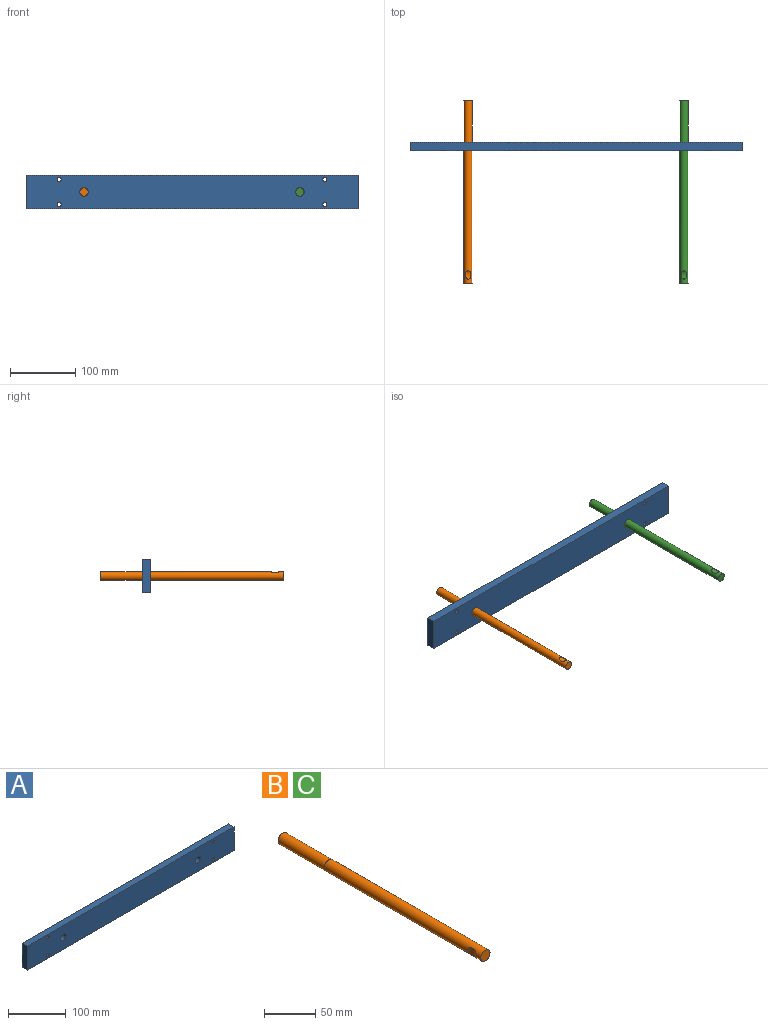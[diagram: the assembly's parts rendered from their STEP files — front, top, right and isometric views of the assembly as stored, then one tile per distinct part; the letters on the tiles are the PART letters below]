
ASSEMBLY  parts=3 mates=1
PART A: 12 faces, bbox 508x12.7x50.8 mm
  f0: plane 508x12.7mm, normal (0,0,-1), area 6451.6mm2, adj f1,f3,f4,f5
  f1: plane 50.8x12.7mm, normal (1,0,0), area 645.2mm2, adj f0,f2,f4,f5
  f2: plane 508x12.7mm, normal (0,0,1), area 6451.6mm2, adj f1,f3,f4,f5
  f3: plane 50.8x12.7mm, normal (-1,0,0), area 645.2mm2, adj f0,f2,f4,f5
  f4: plane 508x50.8mm, normal (0,-1,0), area 25386.6mm2, adj f0,f1,f2,f3,f6,f7,f8,f9
  f5: plane 508x50.8mm, normal (0,1,0), area 25386.6mm2, adj f0,f1,f2,f3,f6,f7,f8,f9
  f6: cylinder r=3.26mm len=12.7mm, axis (0,-1,0), area 260.4mm2, adj f4,f5
  f7: cylinder r=3.26mm len=12.7mm, axis (0,-1,0), area 260.4mm2, adj f4,f5
  f8: cylinder r=3.26mm len=12.7mm, axis (0,-1,0), area 260.4mm2, adj f4,f5
  f9: cylinder r=3.26mm len=12.7mm, axis (0,-1,0), area 260.4mm2, adj f4,f5
  f10: cylinder r=6.75mm len=13.49mm, axis (0,-1,0), area 538.3mm2, adj f4,f5
  f11: cylinder r=6.75mm len=13.49mm, axis (0,-1,0), area 538.3mm2, adj f4,f5
PART B: 6 faces, bbox 12.7x279.4x12.7 mm
  f0: cylinder r=6.35mm len=215.9mm, axis (0,1,0), area 8518.8mm2, adj f1,f2,f4
  f1: plane 12.7x12.7mm, normal (0,-1,0), area 126.7mm2, adj f0
  f2: cylinder r=12.7mm len=12.7mm, axis (0,0,1), area 91.8mm2, adj f0
  f3: cylinder r=6.32mm len=63.5mm, axis (0,1,0), area 2523.4mm2, adj f4,f5
  f4: plane 12.7x12.7mm, normal (0,1,0), area 1mm2, adj f0,f3
  f5: plane 12.65x12.65mm, normal (0,1,0), area 125.7mm2, adj f3
PART C: same geometry as B
PLACE A t=(-134.38,-119.22,31.3)mm
PLACE B rot(axis=(0,1,0),90deg) t=(-299.48,-55.72,31.3)mm
PLACE C rot(axis=(0,1,0),90deg) t=(30.72,-55.72,31.3)mm
MATE revolute C.f0 <-> A.f10  axis (0,1,0) through (30.72,-119.22,31.3)mm
